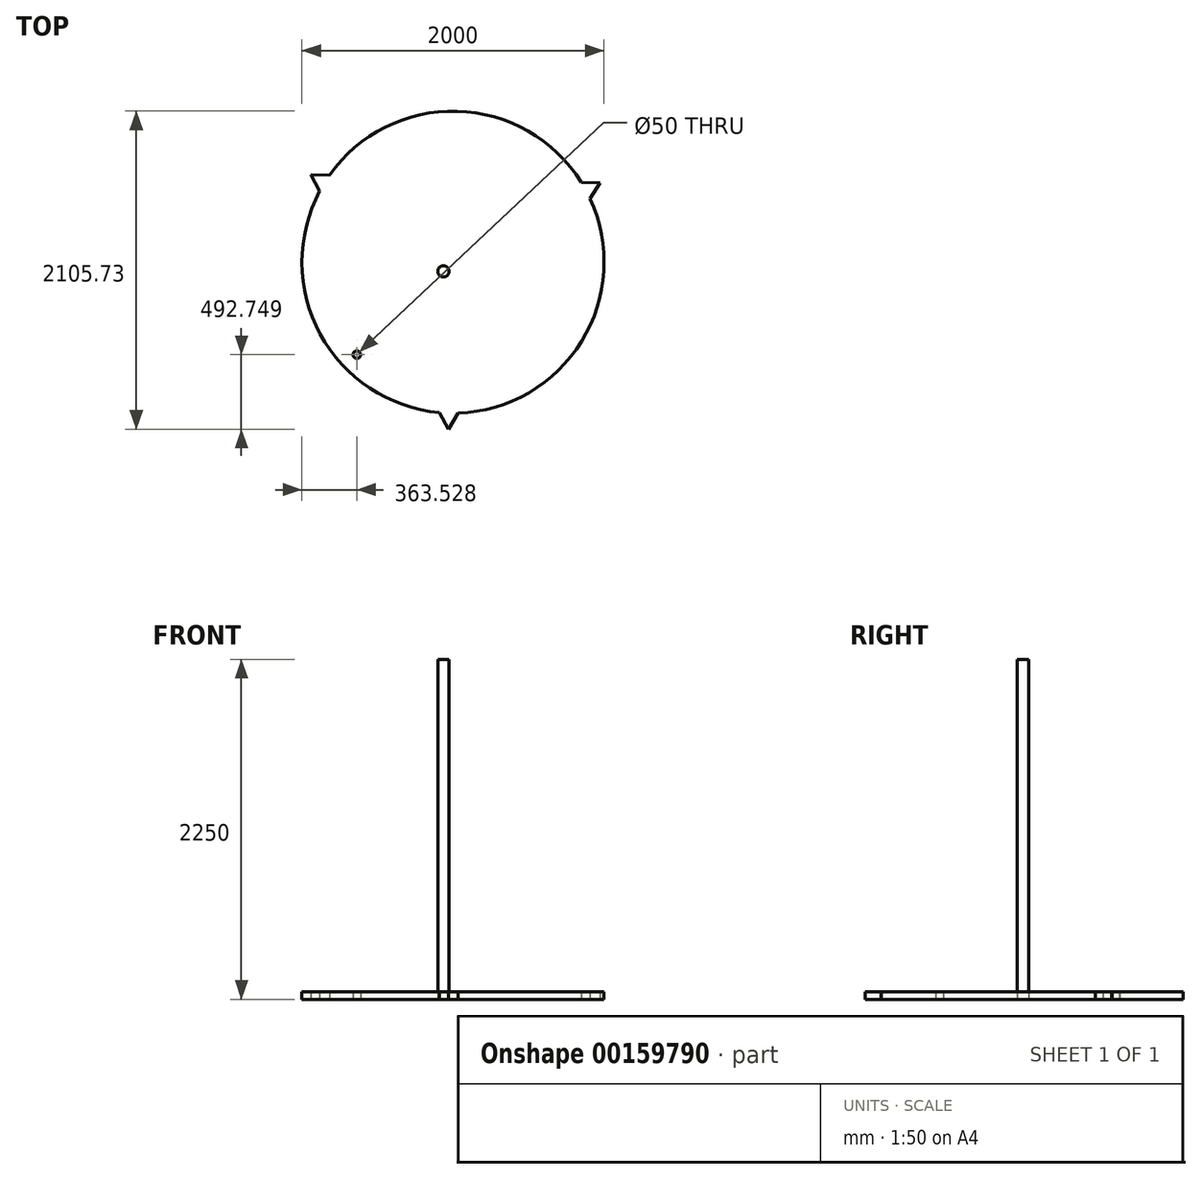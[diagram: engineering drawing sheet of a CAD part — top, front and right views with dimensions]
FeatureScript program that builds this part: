
annotation { "Feature Type Name" : "Feature", "Feature Type Description" : "" }
export const myFeature = defineFeature(function(context is Context, id is Id, definition is map)
    precondition{}
    {
        {
            var Q0;
            Q0=qCreatedBy(makeId("Top.planeOp"),FACE);
            var sketch = newSketch(context, id + "F0", { "sketchPlane" : qUnion([Q0])});
            skCircle(sketch, "E0", {"center": v(-63.65, -61.3) * mm, "radius": 2.5 * mm});
            skCircle(sketch, "E1.cCircle", {"center": v(0, 0) * mm, "radius": 55.3 * mm, "construction": true});
            skLineSegment(sketch, "E1.0", {"start": v(97.3, 52.61) * mm, "end": v(-3.08, -110.57) * mm});
            skLineSegment(sketch, "E1.1", {"start": v(-3.08, -110.57) * mm, "end": v(-94.22, 57.96) * mm});
            skLineSegment(sketch, "E1.2", {"start": v(-94.22, 57.96) * mm, "end": v(97.3, 52.61) * mm});
            skPoint(sketch, "E1.0.midPoint", {"position": v(47.1, -28.98) * mm});
            skCircle(sketch, "E2", {"center": v(0, 0) * mm, "radius": 100 * mm});
            skSolve(sketch);
        }
        {
            var Q0;
            Q0=makeQuery(id+"F0.imprint","IMPRINT",FACE,{"disambiguationData":[TD([[makeQuery(id+"F0.imprint","IMPRINT",EDGE,{"derivedFrom":sQuery(id+"F0.wireOp",EDGE,"E1.0")}),-1.0]])]});
            var Q1;
            {var subQ0=sQuery(id+"F0.wireOp",EDGE,"E2");var subQ1=sQuery(id+"F0.wireOp",EDGE,"E1.0");var subQ2=makeQuery(id+"F0.imprint","INTERSECT",VERTEX,{"disambiguationData":[OD(0.0)],"derivedFrom":[subQ1,subQ0]});Q1=makeQuery(id+"F0.imprint","IMPRINT",FACE,{"disambiguationData":[TD([[makeQuery(id+"F0.imprint","IMPRINT",EDGE,{"disambiguationData":[TD([[subQ2,-1.0]])],"derivedFrom":subQ1}),-1.0]])]});}
            var Q2;
            {var subQ0=sQuery(id+"F0.wireOp",EDGE,"E2");var subQ1=sQuery(id+"F0.wireOp",EDGE,"E1.2");var subQ2=makeQuery(id+"F0.imprint","INTERSECT",VERTEX,{"disambiguationData":[OD(0.0)],"derivedFrom":[subQ1,subQ0]});Q2=makeQuery(id+"F0.imprint","IMPRINT",FACE,{"disambiguationData":[TD([[makeQuery(id+"F0.imprint","IMPRINT",EDGE,{"disambiguationData":[TD([[subQ2,-1.0]])],"derivedFrom":subQ1}),1.0]])]});}
            var Q3;
            {var subQ0=sQuery(id+"F0.wireOp",EDGE,"E2");var subQ1=sQuery(id+"F0.wireOp",EDGE,"E1.0");var subQ2=makeQuery(id+"F0.imprint","INTERSECT",VERTEX,{"disambiguationData":[OD(0.0)],"derivedFrom":[subQ1,subQ0]});Q3=makeQuery(id+"F0.imprint","IMPRINT",FACE,{"disambiguationData":[TD([[makeQuery(id+"F0.imprint","IMPRINT",EDGE,{"disambiguationData":[TD([[subQ2,-1.0]])],"derivedFrom":subQ1}),1.0]])]});}
            var Q4;
            Q4=makeQuery(id+"F0.imprint","IMPRINT",FACE,{"disambiguationData":[TD([[makeQuery(id+"F0.imprint","IMPRINT",EDGE,{"derivedFrom":sQuery(id+"F0.wireOp",EDGE,"E0")}),-1.0]])]});
            var Q5;
            {var subQ0=sQuery(id+"F0.wireOp",EDGE,"E1.2");var subQ1=sQuery(id+"F0.wireOp",EDGE,"E1.1");var subQ2=makeQuery(id+"F0.imprint","INTERSECT",VERTEX,{"derivedFrom":[subQ1,subQ0]});Q5=makeQuery(id+"F0.imprint","IMPRINT",FACE,{"disambiguationData":[TD([[makeQuery(id+"F0.imprint","IMPRINT",EDGE,{"disambiguationData":[TD([[subQ2,1.0]])],"derivedFrom":subQ1}),-1.0]])]});}
            extrude(context, id + "F1", {"entities" : qUnion([Q0, Q1, Q2, Q3, Q4, Q5]), "depth" : 5 * mm});
        }
        {
            var Q0;
            Q0=makeQuery(id+"F0.imprint","IMPRINT",FACE,{"disambiguationData":[TD([[makeQuery(id+"F0.imprint","IMPRINT",EDGE,{"derivedFrom":sQuery(id+"F0.wireOp",EDGE,"E0")}),1.0]])]});
            var Q1;
            Q1=sQuery(id+"F0.wireOp",EDGE,"E0");
            extrude(context, id + "F2", {"entities" : qUnion([Q0]), "surfaceEntities" : qUnion([Q1]), "depth" : 150 * mm});
        }
        {
            var Q0;
            Q0=makeQuery(id+"F2.opExtrude","SWEPT_BODY",BODY,{"disambiguationData":[OSD([sQuery(id+"F0.wireOp",EDGE,"E0")])]});
            var Q1;
            Q1=sQuery(id+"F0.wireOp",VERTEX,"E0.center");
            transform(context, id + "F3", {"entities" : qUnion([Q0]), "transformType" : TransformType.SCALE_UNIFORMLY, "scale" : 10, "scalePoint" : qUnion([Q1]), "makeCopy" : false});
        }
        {
            var Q0;
            Q0=makeQuery(id+"F1.opExtrude","SWEPT_BODY",BODY,{"disambiguationData":[OSD([sQuery(id+"F0.wireOp",EDGE,"E1.0"),sQuery(id+"F0.wireOp",EDGE,"E1.1"),sQuery(id+"F0.wireOp",EDGE,"E1.2")])]});
            var Q1;
            Q1=sQuery(id+"F0.wireOp",VERTEX,"E1.cCircle.center");
            transform(context, id + "F4", {"entities" : qUnion([Q0]), "transformType" : TransformType.SCALE_UNIFORMLY, "scale" : 10, "scalePoint" : qUnion([Q1]), "makeCopy" : false});
        }
        {
            var Q0;
            Q0=makeQuery(id+"F2.opExtrude","SWEPT_BODY",BODY,{"disambiguationData":[OSD([sQuery(id+"F0.wireOp",EDGE,"E0")])]});
            var Q1;
            Q1=sQuery(id+"F0.wireOp",VERTEX,"E0.center");
            transform(context, id + "F5", {"entities" : qUnion([Q0]), "transformType" : TransformType.SCALE_UNIFORMLY, "scale" : 1.5, "scalePoint" : qUnion([Q1]), "makeCopy" : false});
        }
    });
